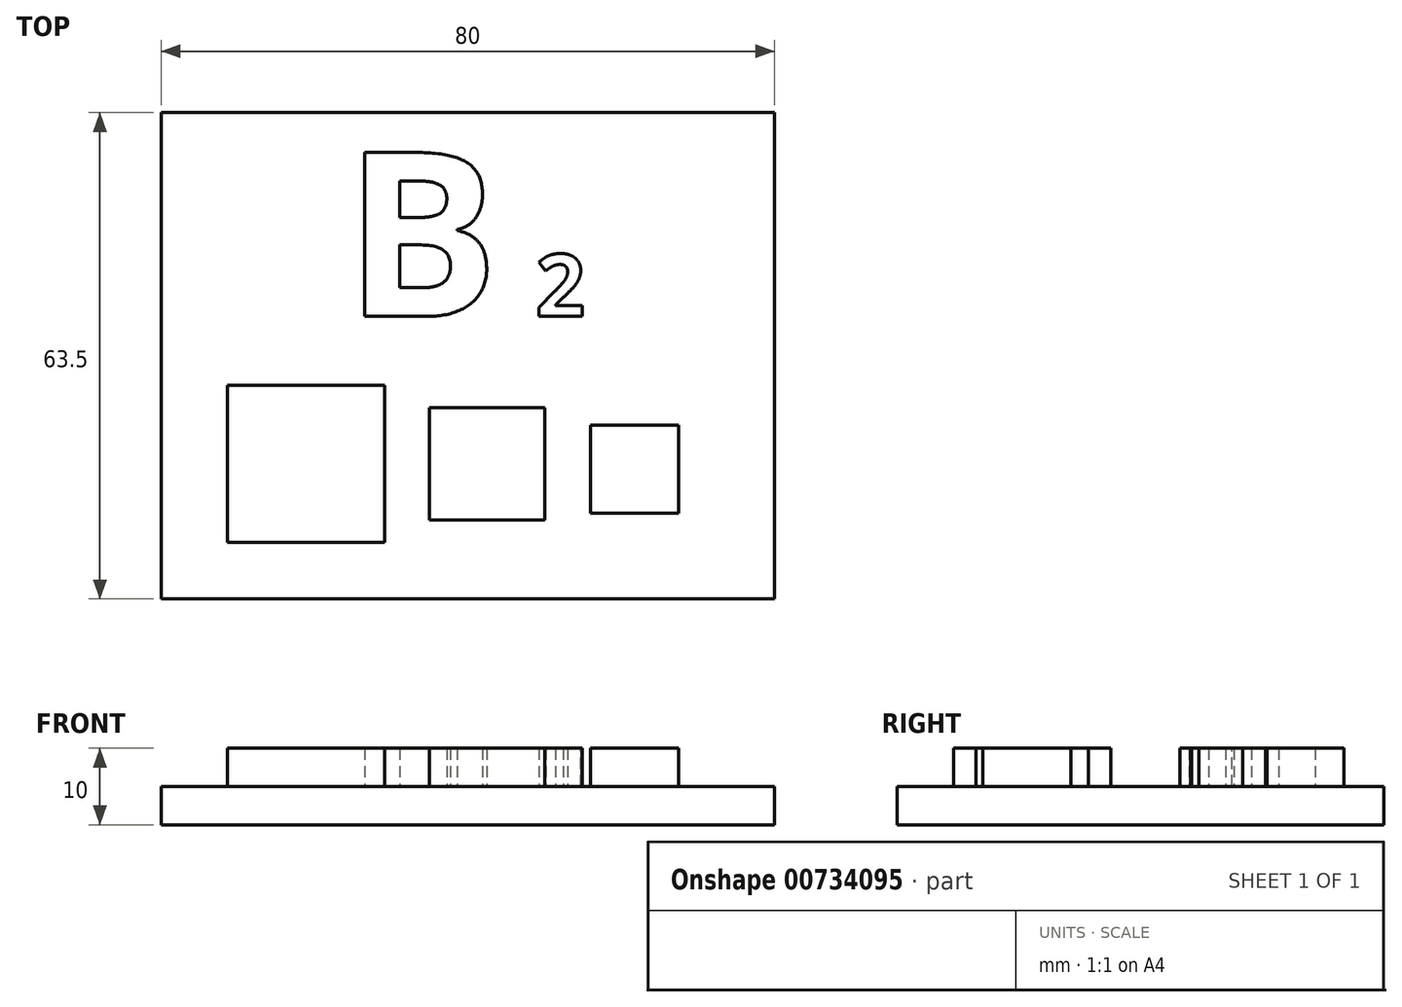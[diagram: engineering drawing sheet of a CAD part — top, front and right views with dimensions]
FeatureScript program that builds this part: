
annotation { "Feature Type Name" : "Feature", "Feature Type Description" : "" }
export const myFeature = defineFeature(function(context is Context, id is Id, definition is map)
    precondition{}
    {
        {
            var Q0;
            Q0=qCreatedBy(makeId("Top.planeOp"),FACE);
            var sketch = newSketch(context, id + "F0", { "sketchPlane" : qUnion([Q0])});
            skLineSegment(sketch, "E0.bottom", {"start": v(40, -33.5) * mm, "end": v(-40, -33.5) * mm});
            skLineSegment(sketch, "E0.top", {"start": v(40, 30) * mm, "end": v(-40, 30) * mm});
            skLineSegment(sketch, "E0.left", {"start": v(40, -30) * mm, "end": v(40, 30) * mm});
            skLineSegment(sketch, "E0.right", {"start": v(-40, -30) * mm, "end": v(-40, 30) * mm});
            skPoint(sketch, "E0.middle", {"position": v(0, 0) * mm});
            skLineSegment(sketch, "E1", {"start": v(-40, -32.5) * mm, "end": v(-40, -30) * mm});
            skLineSegment(sketch, "E2", {"start": v(40, -32.5) * mm, "end": v(40, -30) * mm});
            skLineSegment(sketch, "E3", {"start": v(-40, -33.5) * mm, "end": v(-40, -32.5) * mm});
            skLineSegment(sketch, "E4", {"start": v(40, -33.5) * mm, "end": v(40, -32.5) * mm});
            skSolve(sketch);
        }
        {
            var Q0;
            Q0=qCreatedBy(makeId("Top.planeOp"),FACE);
            var sketch = newSketch(context, id + "F1", { "sketchPlane" : qUnion([Q0])});
            skLineSegment(sketch, "E5.bottom", {"start": v(34.1, 29.06) * mm, "end": v(-37, 29.06) * mm});
            skLineSegment(sketch, "E5.top", {"start": v(34.1, -33.44) * mm, "end": v(-37, -33.44) * mm});
            skLineSegment(sketch, "E5.left", {"start": v(34.1, 29.06) * mm, "end": v(34.1, -30.94) * mm});
            skLineSegment(sketch, "E5.right", {"start": v(-39.5, 29.06) * mm, "end": v(-39.5, -30.94) * mm});
            skLineSegment(sketch, "E6", {"start": v(-39.5, 29.06) * mm, "end": v(-37, 29.06) * mm});
            skLineSegment(sketch, "E7", {"start": v(31.6, 29.06) * mm, "end": v(34.1, 29.06) * mm});
            skLineSegment(sketch, "E8", {"start": v(34.1, -30.94) * mm, "end": v(34.1, -33.44) * mm});
            skLineSegment(sketch, "E9", {"start": v(34.1, -33.44) * mm, "end": v(31.6, -33.44) * mm});
            skLineSegment(sketch, "E10", {"start": v(-39.5, -30.94) * mm, "end": v(-39.5, -33.44) * mm});
            skLineSegment(sketch, "E11", {"start": v(-39.5, -33.44) * mm, "end": v(-37, -33.44) * mm});
            skLineSegment(sketch, "E12.bottom", {"start": v(-10.83, -26.13) * mm, "end": v(-31.37, -26.13) * mm});
            skLineSegment(sketch, "E12.top", {"start": v(-10.83, -5.59) * mm, "end": v(-31.37, -5.59) * mm});
            skLineSegment(sketch, "E12.left", {"start": v(-10.83, -26.13) * mm, "end": v(-10.83, -5.59) * mm});
            skLineSegment(sketch, "E12.right", {"start": v(-31.37, -26.13) * mm, "end": v(-31.37, -5.59) * mm});
            skPoint(sketch, "E12.middle", {"position": v(-21.1, -15.86) * mm});
            skLineSegment(sketch, "E13.bottom", {"start": v(10, -23.2) * mm, "end": v(-5, -23.2) * mm});
            skLineSegment(sketch, "E13.top", {"start": v(10, -8.52) * mm, "end": v(-5, -8.52) * mm});
            skLineSegment(sketch, "E13.left", {"start": v(10, -23.2) * mm, "end": v(10, -8.52) * mm});
            skLineSegment(sketch, "E13.right", {"start": v(-5, -23.2) * mm, "end": v(-5, -8.52) * mm});
            skPoint(sketch, "E13.middle", {"position": v(2.5, -15.86) * mm});
            skLineSegment(sketch, "E14", {"start": v(2.5, -15.86) * mm, "end": v(2.5, -15.86) * mm});
            skPoint(sketch, "E14.endSnap0", {"position": v(10, -15.86) * mm});
            skLineSegment(sketch, "E15.bottom", {"start": v(27.47, -22.3) * mm, "end": v(15.97, -22.3) * mm});
            skLineSegment(sketch, "E15.top", {"start": v(27.47, -10.8) * mm, "end": v(15.97, -10.8) * mm});
            skLineSegment(sketch, "E15.left", {"start": v(27.47, -22.3) * mm, "end": v(27.47, -10.8) * mm});
            skLineSegment(sketch, "E15.right", {"start": v(15.97, -22.3) * mm, "end": v(15.97, -10.8) * mm});
            skPoint(sketch, "E15.middle", {"position": v(21.72, -16.54) * mm});
            skText(sketch, "E16", { "text": "B", "fontName": "OpenSans-Bold.ttf"});
            skText(sketch, "E17", { "text": "2", "fontName": "OpenSans-Bold.ttf"});
            const initialGuessF1  = {"E16": [-0.01613, 0.00338, 1, 0, 0.0216], "E17": [0.00882, 0.00338, 1, 0, 0.00818]};
            skSetInitialGuess(sketch, initialGuessF1);
            skSolve(sketch);
        }
        {
            var Q0;
            Q0=makeQuery(id+"F1.imprint","IMPRINT",FACE,{"disambiguationData":[TD([[makeQuery(id+"F1.imprint","IMPRINT",EDGE,{"derivedFrom":sQuery(id+"F1.wireOp",EDGE,"8c178970-5c55-42ac-8938-7c1ab3ab2c94.sketch_text.stroke-0")}),-1.0]])]});
            var Q1;
            Q1=makeQuery(id+"F1.imprint","IMPRINT",FACE,{"disambiguationData":[TD([[makeQuery(id+"F1.imprint","IMPRINT",EDGE,{"derivedFrom":sQuery(id+"F1.wireOp",EDGE,"8c178970-5c55-42ac-8938-7c1ab3ab2c94.sketch_text.stroke-12")}),-1.0]])]});
            var Q2;
            Q2=makeQuery(id+"F1.imprint","IMPRINT",FACE,{"disambiguationData":[TD([[makeQuery(id+"F1.imprint","IMPRINT",EDGE,{"derivedFrom":sQuery(id+"F1.wireOp",EDGE,"8c178970-5c55-42ac-8938-7c1ab3ab2c94.sketch_text.stroke-24")}),-1.0]])]});
            var Q3;
            Q3=makeQuery(id+"F1.imprint","IMPRINT",FACE,{"disambiguationData":[TD([[makeQuery(id+"F1.imprint","IMPRINT",EDGE,{"derivedFrom":sQuery(id+"F1.wireOp",EDGE,"E12.bottom")}),-1.0]])]});
            var Q4;
            Q4=makeQuery(id+"F1.imprint","IMPRINT",FACE,{"disambiguationData":[TD([[makeQuery(id+"F1.imprint","IMPRINT",EDGE,{"derivedFrom":sQuery(id+"F1.wireOp",EDGE,"E13.bottom")}),-1.0]])]});
            var Q5;
            Q5=makeQuery(id+"F1.imprint","IMPRINT",FACE,{"disambiguationData":[TD([[makeQuery(id+"F1.imprint","IMPRINT",EDGE,{"derivedFrom":sQuery(id+"F1.wireOp",EDGE,"E15.bottom")}),-1.0]])]});
            var Q6;
            Q6=makeQuery(id+"F1.imprint","IMPRINT",FACE,{"disambiguationData":[TD([[makeQuery(id+"F1.imprint","IMPRINT",EDGE,{"derivedFrom":sQuery(id+"F1.wireOp",EDGE,"E17.sketch_text.stroke-0")}),-1.0]])]});
            var Q7;
            Q7=makeQuery(id+"F1.imprint","IMPRINT",FACE,{"disambiguationData":[TD([[makeQuery(id+"F1.imprint","IMPRINT",EDGE,{"derivedFrom":sQuery(id+"F1.wireOp",EDGE,"E16.sketch_text.stroke-0")}),-1.0]])]});
            extrude(context, id + "F2", {"entities" : qUnion([Q0, Q1, Q2, Q3, Q4, Q5, Q6, Q7]), "depth" : 10 * mm, "offsetDistance" : 25 * mm});
        }
        {
            var Q0;
            Q0 = qSketchRegion(id + "F0", true);
            extrude(context, id + "F3", {"entities" : qUnion([Q0]), "operationType" : NewBodyOperationType.ADD, "depth" : 5 * mm, "offsetDistance" : 25 * mm});
        }
    });
